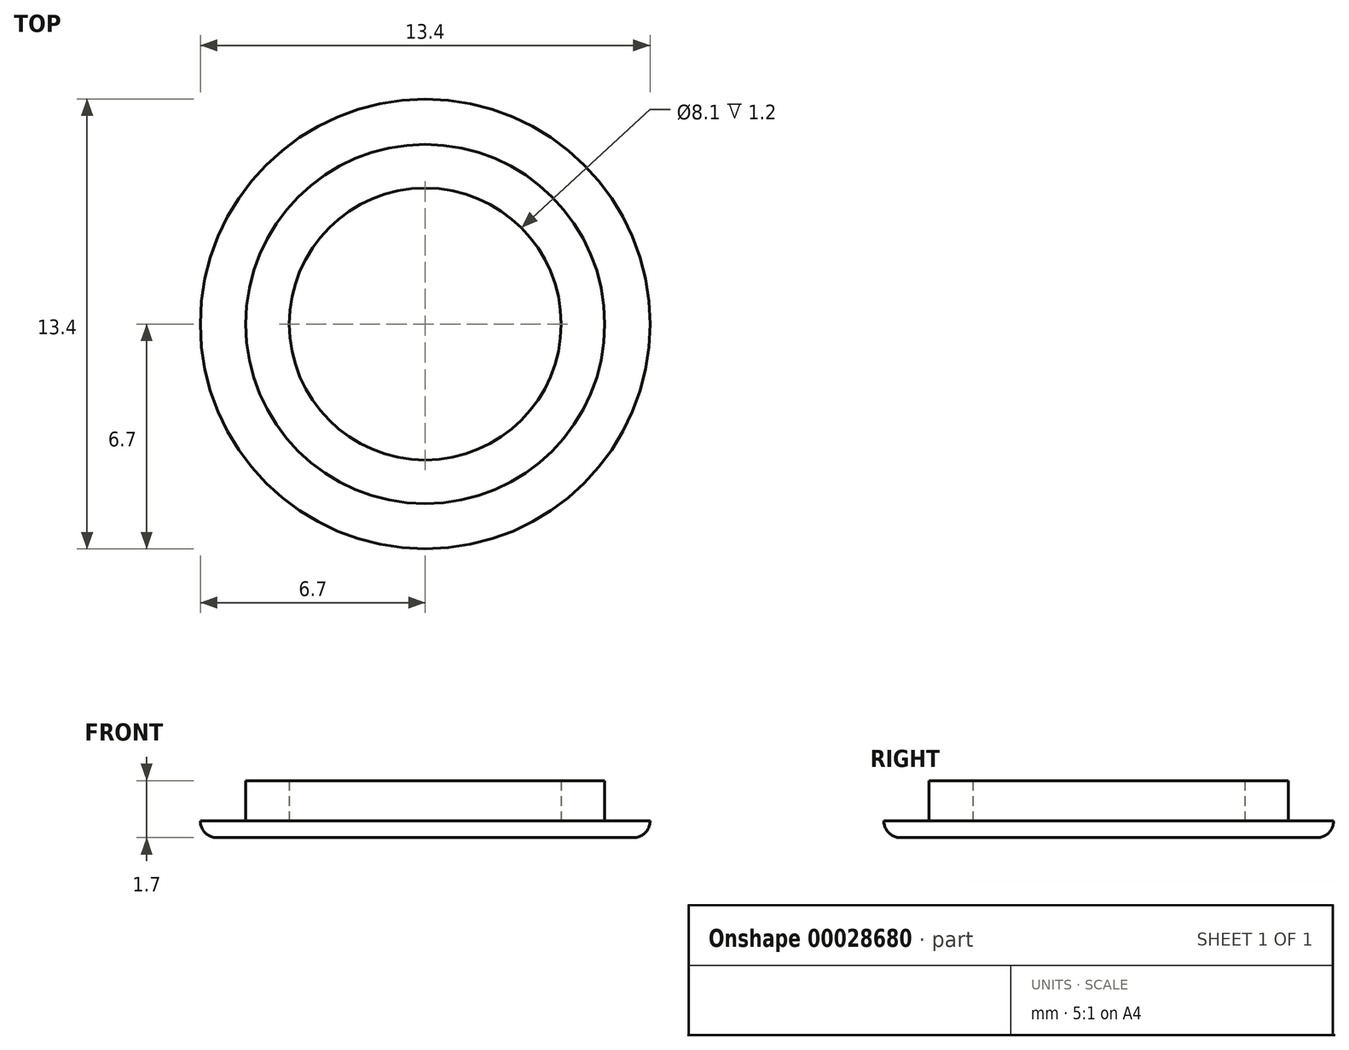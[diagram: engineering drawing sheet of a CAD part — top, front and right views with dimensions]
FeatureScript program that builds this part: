
annotation { "Feature Type Name" : "Feature", "Feature Type Description" : "" }
export const myFeature = defineFeature(function(context is Context, id is Id, definition is map)
    precondition{}
    {
        {
            var Q0;
            Q0=qCreatedBy(makeId("Top.planeOp"),FACE);
            var sketch = newSketch(context, id + "F0", { "sketchPlane" : qUnion([Q0])});
            skCircle(sketch, "E0", {"center": v(0, 0) * mm, "radius": 6.7 * mm});
            skSolve(sketch);
        }
        {
            var Q0;
            Q0 = qSketchRegion(id + "F0", true);
            extrude(context, id + "F1", {"entities" : qUnion([Q0]), "depth" : 0.5 * mm, "offsetDistance" : 25 * mm});
        }
        {
            var Q0;
            Q0=makeQuery(id+"F1.opExtrude","CAP_FACE",FACE,{"disambiguationData":[OSD([sQuery(id+"F0.wireOp",EDGE,"E0")])],"isStart":false});
            var sketch = newSketch(context, id + "F2", { "sketchPlane" : qUnion([Q0])});
            skCircle(sketch, "E1", {"center": v(0, 0) * mm, "radius": 5.35 * mm});
            skCircle(sketch, "E2", {"center": v(0, 0) * mm, "radius": 4.05 * mm});
            skSolve(sketch);
        }
        {
            var Q0;
            Q0 = qSketchRegion(id + "F2", true);
            extrude(context, id + "F3", {"entities" : qUnion([Q0]), "operationType" : NewBodyOperationType.ADD, "depth" : 1.2 * mm, "offsetDistance" : 25 * mm});
        }
        {
            var Q0;
            Q0=makeQuery(id+"F1.opExtrude","CAP_EDGE",EDGE,{"disambiguationData":[OSD([sQuery(id+"F0.wireOp",EDGE,"E0")])],"isStart":true});
            fillet(context, id + "F4", {"entities" : qUnion([Q0]), "radius" : 0.5 * mm, "tangentPropagation" : true, "defaultsChanged" : true, "vertexSettings" : [], "allowEdgeOverflow" : false});
        }
    });
